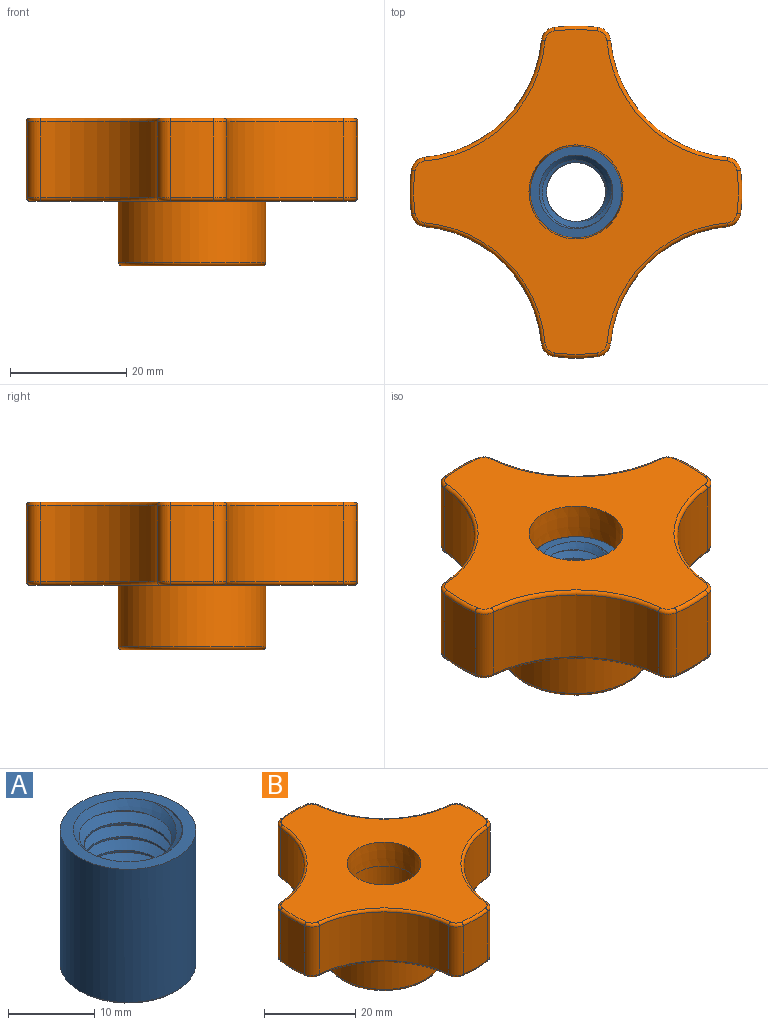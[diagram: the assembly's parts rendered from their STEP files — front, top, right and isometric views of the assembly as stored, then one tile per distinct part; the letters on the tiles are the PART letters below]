
ASSEMBLY  parts=2 mates=1
PART A: 10 faces, bbox 15.7x15.7x20.5 mm
  f0: cone r=6.35mm half-angle=45deg, axis (0,0,1), area 33.1mm2, adj f5,f6,f7,f9
  f1: cone r=6.6mm half-angle=45deg, axis (0,0,-1), area 47.7mm2, adj f3,f5,f6,f7,f8
  f2: cone r=7.62mm half-angle=45deg, axis (0,0,1), area 17.5mm2, adj f4,f8
  f3: cylinder r=6.35mm len=18.9mm, axis (0,0,1), area 94.2mm2, adj f1,f6,f7,f9
  f4: cylinder r=7.87mm len=18.9mm, axis (0,0,-1), area 934.8mm2, adj f2,f9
  f5: cylinder r=5.08mm len=16.36mm, axis (0,0,1), area 76.6mm2, adj f0,f1,f6,f7
  f6: bspline ~19.69x13.35mm, area 472.5mm2, adj f0,f1,f3,f5
  f7: bspline ~19.88x13.35mm, area 476.6mm2, adj f0,f1,f3,f5
  f8: plane 15.24x15.24mm, normal (0,0,-1), area 45.4mm2, adj f1,f2
  f9: plane 15.75x15.75mm, normal (0,0,1), area 68.1mm2, adj f0,f3,f4
PART B: 56 faces, bbox 57.7x57.7x25.4 mm
  f0: cone r=7.87mm half-angle=2deg, axis (0,0,1), area 313.7mm2, adj f7,f8
  f1: torus R=27.94mm, axis (0,0,-1), area 7.5mm2, adj f8,f12,f34,f37
  f2: torus R=27.94mm, axis (0,0,1), area 7.5mm2, adj f6,f9,f47,f53
  f3: torus R=12.06mm, axis (0,0,1), area 78.1mm2, adj f5,f13
  f4: cone r=7.87mm half-angle=45deg, axis (0,0,-1), area 18.1mm2, adj f7,f13
  f5: cylinder r=12.7mm len=25.4mm, axis (0,0,1), area 836.1mm2, adj f3,f9
  f6: cylinder r=28.57mm len=13.02mm, axis (0,0,1), area 98.4mm2, adj f2,f31,f48,f54
  f7: cylinder r=7.87mm len=18.9mm, axis (0,0,1), area 934.8mm2, adj f0,f4
  f8: plane 55.88x55.88mm, normal (0,0,1), area 1289mm2, adj f0,f1,f25,f26,f27,f28,f29,f30
  f9: plane 55.88x55.88mm, normal (0,0,-1), area 988mm2, adj f2,f5,f18,f19,f20,f21,f22,f23
  f10: cylinder r=28.57mm len=13.02mm, axis (0,0,1), area 98.4mm2, adj f21,f27,f39,f51
  f11: cylinder r=28.57mm len=13.02mm, axis (0,0,1), area 98.4mm2, adj f22,f28,f42,f45
  f12: cylinder r=28.57mm len=13.02mm, axis (0,0,1), area 98.4mm2, adj f1,f18,f33,f36
  f13: plane 24.13x24.13mm, normal (0,0,-1), area 249.8mm2, adj f3,f4
  f14: cylinder r=22.08mm len=20.07mm, axis (0,0,1), area 401.2mm2, adj f24,f30,f45,f48
  f15: cylinder r=22.08mm len=20.07mm, axis (0,0,1), area 401.2mm2, adj f20,f26,f33,f42
  f16: cylinder r=22.08mm len=20.07mm, axis (0,0,1), area 401.2mm2, adj f23,f29,f51,f54
  f17: cylinder r=22.08mm len=20.07mm, axis (0,0,1), area 401.2mm2, adj f19,f25,f36,f39
  f18: torus R=27.94mm, axis (0,0,1), area 7.5mm2, adj f9,f12,f32,f35
  f19: torus R=22.72mm, axis (0,0,1), area 31.1mm2, adj f9,f17,f35,f38
  f20: torus R=22.72mm, axis (0,0,1), area 31.1mm2, adj f9,f15,f32,f41
  f21: torus R=27.94mm, axis (0,0,1), area 7.5mm2, adj f9,f10,f38,f50
  f22: torus R=27.94mm, axis (0,0,1), area 7.5mm2, adj f9,f11,f41,f44
  f23: torus R=22.72mm, axis (0,0,1), area 31.1mm2, adj f9,f16,f50,f53
  f24: torus R=22.72mm, axis (0,0,1), area 31.1mm2, adj f9,f14,f44,f47
  f25: torus R=22.72mm, axis (0,0,-1), area 31.1mm2, adj f8,f17,f37,f40
  f26: torus R=22.72mm, axis (0,0,-1), area 31.1mm2, adj f8,f15,f34,f43
  f27: torus R=27.94mm, axis (0,0,-1), area 7.5mm2, adj f8,f10,f40,f52
  f28: torus R=27.94mm, axis (0,0,-1), area 7.5mm2, adj f8,f11,f43,f46
  f29: torus R=22.72mm, axis (0,0,-1), area 31.1mm2, adj f8,f16,f52,f55
  f30: torus R=22.72mm, axis (0,0,-1), area 31.1mm2, adj f8,f14,f46,f49
  f31: torus R=27.94mm, axis (0,0,-1), area 7.5mm2, adj f6,f8,f49,f55
  f32: torus R=1.91mm, axis (0,0,1), area 3.1mm2, adj f9,f18,f20,f33
  f33: cylinder r=2.54mm len=13.02mm, axis (0,0,-1), area 44.7mm2, adj f12,f15,f32,f34
  f34: torus R=1.91mm, axis (0,0,-1), area 3.1mm2, adj f1,f8,f26,f33
  f35: torus R=1.91mm, axis (0,0,1), area 3.1mm2, adj f9,f18,f19,f36
  f36: cylinder r=2.54mm len=13.02mm, axis (0,0,-1), area 44.7mm2, adj f12,f17,f35,f37
  f37: torus R=1.91mm, axis (0,0,-1), area 3.1mm2, adj f1,f8,f25,f36
  f38: torus R=1.91mm, axis (0,0,1), area 3.1mm2, adj f9,f19,f21,f39
  f39: cylinder r=2.54mm len=13.02mm, axis (0,0,-1), area 44.7mm2, adj f10,f17,f38,f40
  f40: torus R=1.91mm, axis (0,0,-1), area 3.1mm2, adj f8,f25,f27,f39
  f41: torus R=1.91mm, axis (0,0,1), area 3.1mm2, adj f9,f20,f22,f42
  f42: cylinder r=2.54mm len=13.02mm, axis (0,0,-1), area 44.7mm2, adj f11,f15,f41,f43
  f43: torus R=1.91mm, axis (0,0,-1), area 3.1mm2, adj f8,f26,f28,f42
  f44: torus R=1.91mm, axis (0,0,1), area 3.1mm2, adj f9,f22,f24,f45
  f45: cylinder r=2.54mm len=13.02mm, axis (0,0,-1), area 44.7mm2, adj f11,f14,f44,f46
  f46: torus R=1.91mm, axis (0,0,-1), area 3.1mm2, adj f8,f28,f30,f45
  f47: torus R=1.91mm, axis (0,0,1), area 3.1mm2, adj f2,f9,f24,f48
  f48: cylinder r=2.54mm len=13.02mm, axis (0,0,-1), area 44.7mm2, adj f6,f14,f47,f49
  f49: torus R=1.91mm, axis (0,0,-1), area 3.1mm2, adj f8,f30,f31,f48
  f50: torus R=1.91mm, axis (0,0,1), area 3.1mm2, adj f9,f21,f23,f51
  f51: cylinder r=2.54mm len=13.02mm, axis (0,0,-1), area 44.7mm2, adj f10,f16,f50,f52
  f52: torus R=1.91mm, axis (0,0,-1), area 3.1mm2, adj f8,f27,f29,f51
  f53: torus R=1.91mm, axis (0,0,1), area 3.1mm2, adj f2,f9,f23,f54
  f54: cylinder r=2.54mm len=13.02mm, axis (0,0,-1), area 44.7mm2, adj f6,f16,f53,f55
  f55: torus R=1.91mm, axis (0,0,-1), area 3.1mm2, adj f8,f29,f31,f54
PLACE A t=(-5.32,-0.53,64.03)mm
PLACE B t=(-5.32,-0.53,64.03)mm
MATE fastened A.f3 <-> B.f0  axis (0,0,-1) through (-5.32,-0.53,51.33)mm
